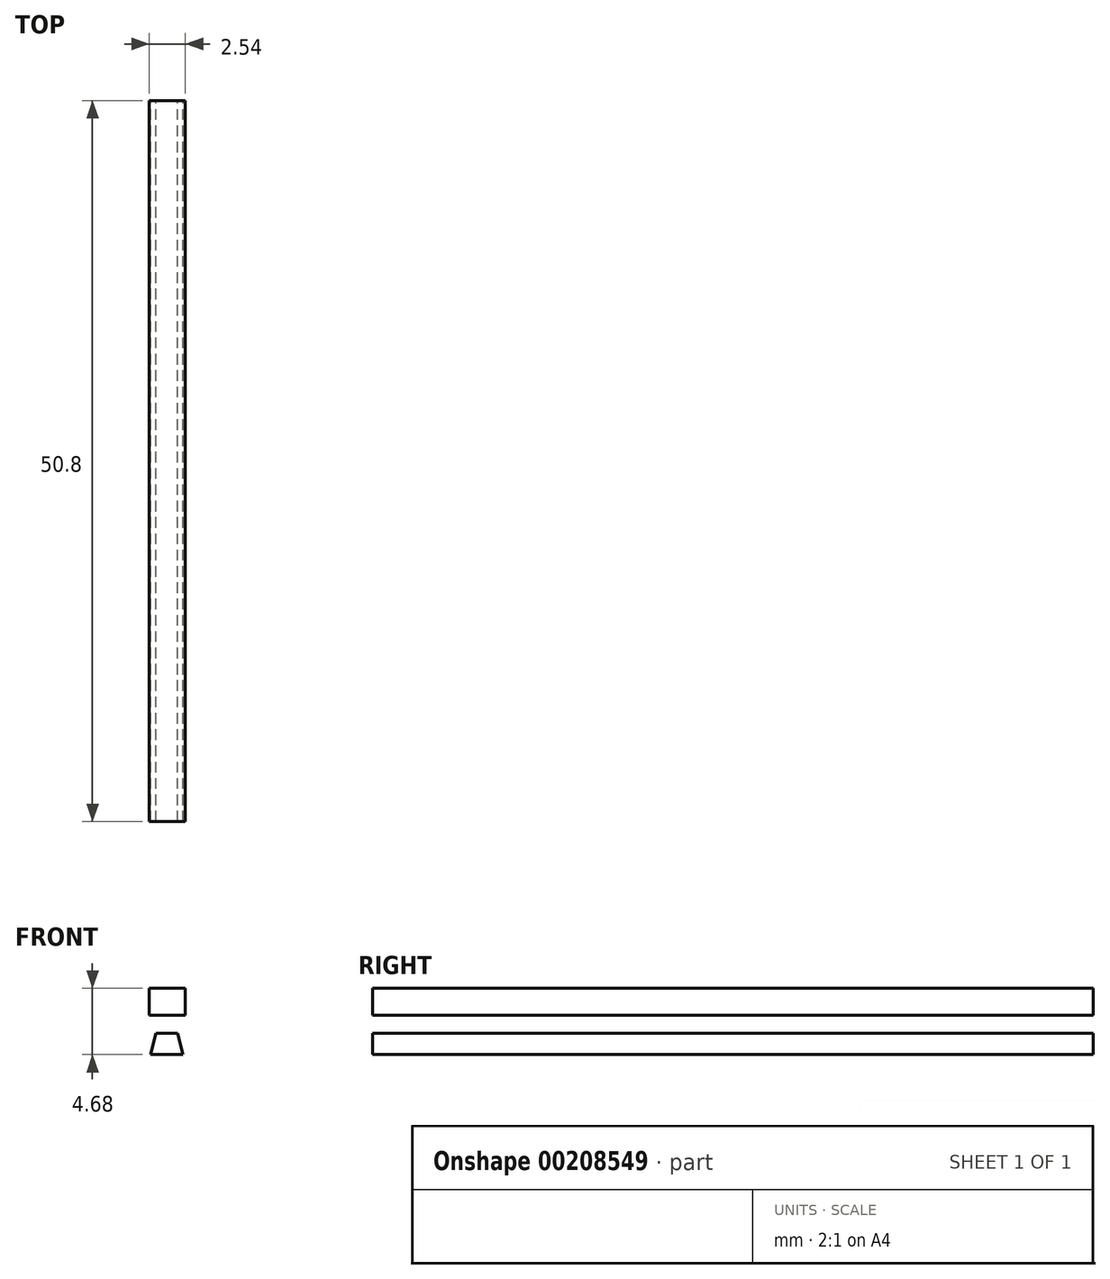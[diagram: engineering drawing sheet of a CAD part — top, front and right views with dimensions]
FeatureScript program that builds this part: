
annotation { "Feature Type Name" : "Feature", "Feature Type Description" : "" }
export const myFeature = defineFeature(function(context is Context, id is Id, definition is map)
    precondition{}
    {
        {
            var Q0;
            Q0=qCreatedBy(makeId("Front.planeOp"),FACE);
            var sketch = newSketch(context, id + "F0", { "sketchPlane" : qUnion([Q0])});
            skLineSegment(sketch, "E0", {"start": v(0, -2.06) * mm, "end": v(1.14, -2.06) * mm});
            skLineSegment(sketch, "E1", {"start": v(0, -2.06) * mm, "end": v(-1.14, -2.06) * mm});
            skLineSegment(sketch, "E2", {"start": v(0, -0.56) * mm, "end": v(0.76, -0.56) * mm});
            skLineSegment(sketch, "E3", {"start": v(0, -0.56) * mm, "end": v(-0.76, -0.56) * mm});
            skLineSegment(sketch, "E4", {"start": v(-0.76, -0.56) * mm, "end": v(-1.14, -2.06) * mm});
            skLineSegment(sketch, "E5", {"start": v(0.76, -0.56) * mm, "end": v(1.14, -2.06) * mm});
            skSolve(sketch);
        }
        {
            var Q0;
            Q0=qCreatedBy(makeId("Front.planeOp"),FACE);
            var sketch = newSketch(context, id + "F1", { "sketchPlane" : qUnion([Q0])});
            skLineSegment(sketch, "E6.bottom", {"start": v(-1.22, 2.62) * mm, "end": v(1.32, 2.62) * mm});
            skLineSegment(sketch, "E6.top", {"start": v(-1.22, 0.71) * mm, "end": v(1.32, 0.71) * mm});
            skLineSegment(sketch, "E6.left", {"start": v(-1.22, 2.62) * mm, "end": v(-1.22, 0.71) * mm});
            skLineSegment(sketch, "E6.right", {"start": v(1.32, 2.62) * mm, "end": v(1.32, 0.71) * mm});
            skSolve(sketch);
        }
        {
            var Q0;
            Q0 = qSketchRegion(id + "F0", true);
            extrude(context, id + "F2", {"entities" : qUnion([Q0]), "depth" : 50.8 * mm});
        }
        {
            var Q0;
            Q0=makeQuery(id+"F1.imprint","IMPRINT",FACE,{"disambiguationData":[TD([[makeQuery(id+"F1.imprint","IMPRINT",EDGE,{"derivedFrom":sQuery(id+"F1.wireOp",EDGE,"E6.bottom")}),-1.0]])]});
            var Q1;
            Q1 = qSketchRegion(id + "F1", true);
            extrude(context, id + "F3", {"entities" : qUnion([Q0, Q1]), "depth" : 50.8 * mm});
        }
    });
